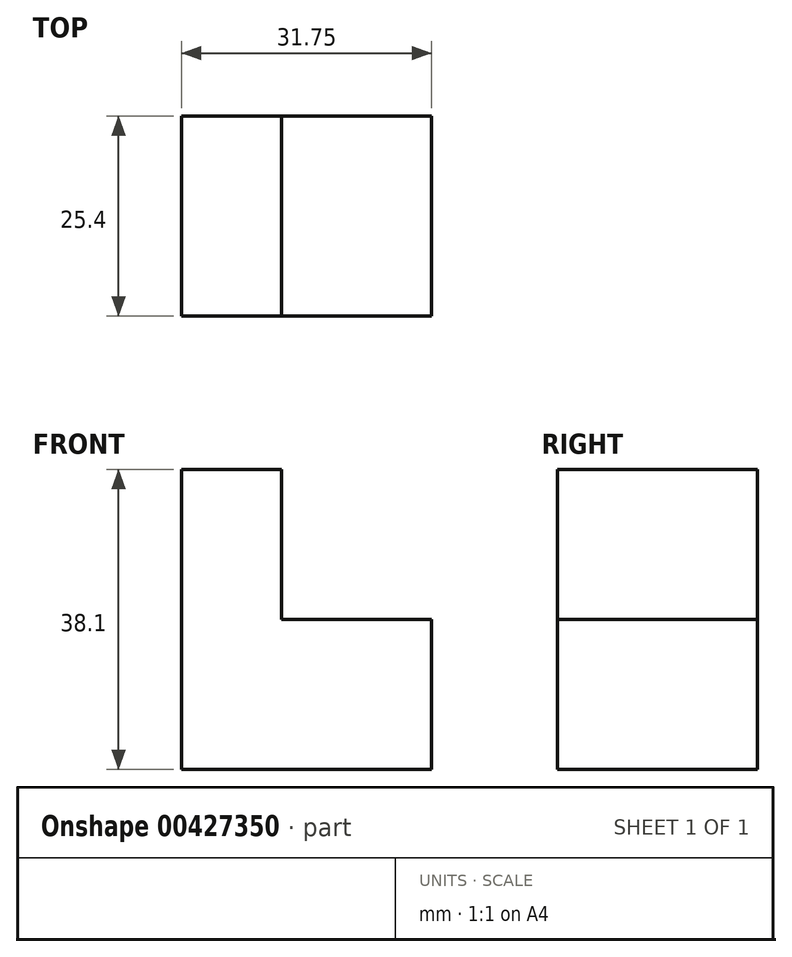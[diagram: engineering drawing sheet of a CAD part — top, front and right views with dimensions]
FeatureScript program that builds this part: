
annotation { "Feature Type Name" : "Feature", "Feature Type Description" : "" }
export const myFeature = defineFeature(function(context is Context, id is Id, definition is map)
    precondition{}
    {
        {
            var Q0;
            Q0=qCreatedBy(makeId("Front.planeOp"),FACE);
            var sketch = newSketch(context, id + "F0", { "sketchPlane" : qUnion([Q0])});
            skLineSegment(sketch, "E0", {"start": v(0, 0) * mm, "end": v(0, 38.1) * mm});
            skLineSegment(sketch, "E1", {"start": v(0, 38.1) * mm, "end": v(12.7, 38.1) * mm});
            skLineSegment(sketch, "E2", {"start": v(12.7, 38.1) * mm, "end": v(12.7, 19.05) * mm});
            skLineSegment(sketch, "E3", {"start": v(12.7, 19.05) * mm, "end": v(31.75, 19.05) * mm});
            skLineSegment(sketch, "E4", {"start": v(31.75, 19.05) * mm, "end": v(31.75, 0) * mm});
            skLineSegment(sketch, "E5", {"start": v(31.75, 0) * mm, "end": v(0, 0) * mm});
            skSolve(sketch);
        }
        {
            var Q0;
            Q0=makeQuery(id+"F0.imprint","IMPRINT",FACE,{"disambiguationData":[TD([[makeQuery(id+"F0.imprint","IMPRINT",EDGE,{"derivedFrom":sQuery(id+"F0.wireOp",EDGE,"E0")}),-1.0]])]});
            extrude(context, id + "F1", {"entities" : qUnion([Q0]), "depth" : 25.4 * mm});
        }
    });
